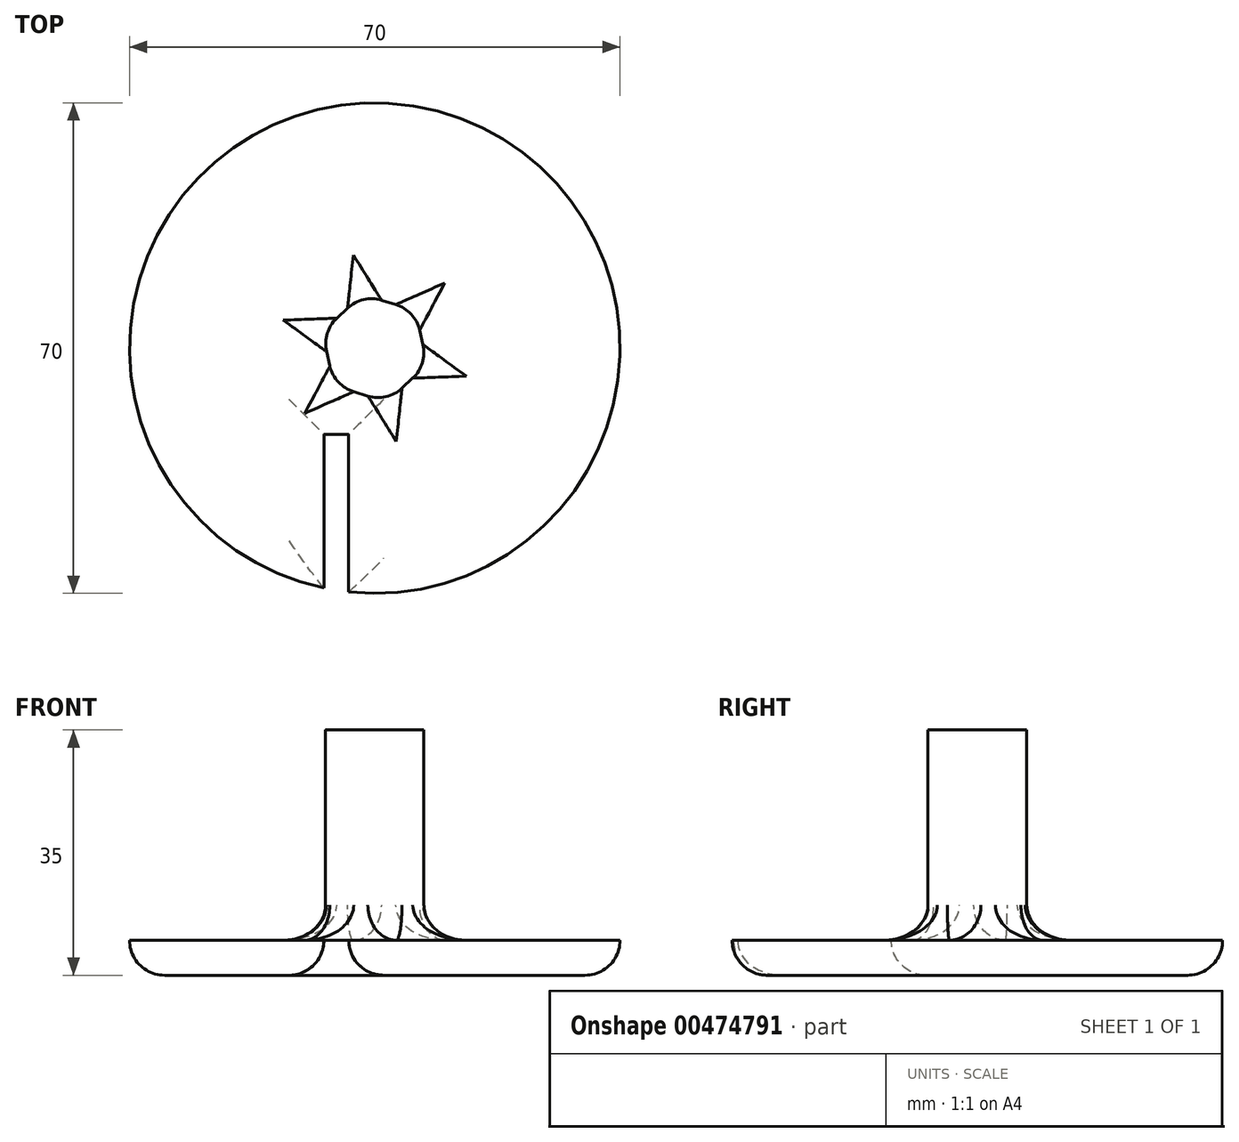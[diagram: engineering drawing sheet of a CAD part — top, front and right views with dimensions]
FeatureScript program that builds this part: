
annotation { "Feature Type Name" : "Feature", "Feature Type Description" : "" }
export const myFeature = defineFeature(function(context is Context, id is Id, definition is map)
    precondition{}
    {
        {
            var Q0;
            Q0=qCreatedBy(makeId("Top.planeOp"),FACE);
            var sketch = newSketch(context, id + "F0", { "sketchPlane" : qUnion([Q0])});
            skCircle(sketch, "E0", {"center": v(0, 0) * mm, "radius": 35 * mm});
            skSolve(sketch);
        }
        {
            var Q0;
            Q0 = qSketchRegion(id + "F0", true);
            extrude(context, id + "F1", {"entities" : qUnion([Q0]), "depth" : 5 * mm});
        }
        {
            var Q0;
            Q0=qCreatedBy(makeId("Top.planeOp"),FACE);
            var sketch = newSketch(context, id + "F2", { "sketchPlane" : qUnion([Q0])});
            skCircle(sketch, "E1.cCircle", {"center": v(0, 0) * mm, "radius": 7.88 * mm, "construction": true});
            skLineSegment(sketch, "E1.0", {"start": v(5.77, 5.37) * mm, "end": v(7.54, -2.3) * mm});
            skLineSegment(sketch, "E1.1", {"start": v(7.54, -2.3) * mm, "end": v(1.77, -7.68) * mm});
            skLineSegment(sketch, "E1.2", {"start": v(1.77, -7.68) * mm, "end": v(-5.77, -5.37) * mm});
            skLineSegment(sketch, "E1.3", {"start": v(-5.77, -5.37) * mm, "end": v(-7.54, 2.3) * mm});
            skLineSegment(sketch, "E1.4", {"start": v(-7.54, 2.3) * mm, "end": v(-1.77, 7.68) * mm});
            skLineSegment(sketch, "E1.5", {"start": v(-1.77, 7.68) * mm, "end": v(5.77, 5.37) * mm});
            skSolve(sketch);
        }
        {
            var Q0;
            Q0 = qSketchRegion(id + "F2", true);
            extrude(context, id + "F3", {"entities" : qUnion([Q0]), "operationType" : NewBodyOperationType.ADD, "depth" : 35 * mm});
        }
        {
            var Q0;
            Q0=makeQuery(id+"F1.opExtrude","CAP_FACE",FACE,{"disambiguationData":[OSD([sQuery(id+"F0.wireOp",EDGE,"E0")])],"isStart":false});
            var sketch = newSketch(context, id + "F4", { "sketchPlane" : qUnion([Q0])});
            skLineSegment(sketch, "E2.bottom", {"start": v(-3.72, -12.29) * mm, "end": v(-7.25, -12.29) * mm});
            skLineSegment(sketch, "E2.top", {"start": v(-3.72, -36.81) * mm, "end": v(-7.25, -36.81) * mm});
            skLineSegment(sketch, "E2.left", {"start": v(-3.72, -12.29) * mm, "end": v(-3.72, -36.81) * mm});
            skLineSegment(sketch, "E2.right", {"start": v(-7.25, -12.29) * mm, "end": v(-7.25, -36.81) * mm});
            skSolve(sketch);
        }
        {
            var Q0;
            Q0 = qSketchRegion(id + "F4", true);
            extrude(context, id + "F5", {"entities" : qUnion([Q0]), "operationType" : NewBodyOperationType.REMOVE, "oppositeDirection" : true, "depth" : 5 * mm});
        }
        {
            var Q0;
            Q0=makeQuery(id+"F3.boolean.opBoolean","INTERSECT",EDGE,{"derivedFrom":[makeQuery(id+"F1.opExtrude","CAP_FACE",FACE,{"disambiguationData":[OSD([sQuery(id+"F0.wireOp",EDGE,"E0")])],"isStart":false}),makeQuery(id+"F3.opExtrude","SWEPT_FACE",FACE,{"disambiguationData":[OSD([sQuery(id+"F2.wireOp",EDGE,"E1.0")])]})]});
            var Q1;
            Q1=makeQuery(id+"F3.boolean.opBoolean","INTERSECT",EDGE,{"derivedFrom":[makeQuery(id+"F1.opExtrude","CAP_FACE",FACE,{"disambiguationData":[OSD([sQuery(id+"F0.wireOp",EDGE,"E0")])],"isStart":false}),makeQuery(id+"F3.opExtrude","SWEPT_FACE",FACE,{"disambiguationData":[OSD([sQuery(id+"F2.wireOp",EDGE,"E1.1")])]})]});
            var Q2;
            Q2=makeQuery(id+"F3.boolean.opBoolean","INTERSECT",EDGE,{"derivedFrom":[makeQuery(id+"F1.opExtrude","CAP_FACE",FACE,{"disambiguationData":[OSD([sQuery(id+"F0.wireOp",EDGE,"E0")])],"isStart":false}),makeQuery(id+"F3.opExtrude","SWEPT_FACE",FACE,{"disambiguationData":[OSD([sQuery(id+"F2.wireOp",EDGE,"E1.4")])]})]});
            var Q3;
            Q3=makeQuery(id+"F3.boolean.opBoolean","INTERSECT",EDGE,{"derivedFrom":[makeQuery(id+"F1.opExtrude","CAP_FACE",FACE,{"disambiguationData":[OSD([sQuery(id+"F0.wireOp",EDGE,"E0")])],"isStart":false}),makeQuery(id+"F3.opExtrude","SWEPT_FACE",FACE,{"disambiguationData":[OSD([sQuery(id+"F2.wireOp",EDGE,"E1.3")])]})]});
            var Q4;
            Q4=makeQuery(id+"F3.boolean.opBoolean","INTERSECT",EDGE,{"derivedFrom":[makeQuery(id+"F1.opExtrude","CAP_FACE",FACE,{"disambiguationData":[OSD([sQuery(id+"F0.wireOp",EDGE,"E0")])],"isStart":false}),makeQuery(id+"F3.opExtrude","SWEPT_FACE",FACE,{"disambiguationData":[OSD([sQuery(id+"F2.wireOp",EDGE,"E1.2")])]})]});
            var Q5;
            Q5=makeQuery(id+"F1.opExtrude","CAP_FACE",FACE,{"disambiguationData":[OSD([sQuery(id+"F0.wireOp",EDGE,"E0")])],"isStart":true});
            var Q6;
            Q6=makeQuery(id+"F3.boolean.opBoolean","INTERSECT",EDGE,{"derivedFrom":[makeQuery(id+"F1.opExtrude","CAP_FACE",FACE,{"disambiguationData":[OSD([sQuery(id+"F0.wireOp",EDGE,"E0")])],"isStart":false}),makeQuery(id+"F3.opExtrude","SWEPT_FACE",FACE,{"disambiguationData":[OSD([sQuery(id+"F2.wireOp",EDGE,"E1.5")])]})]});
            fillet(context, id + "F6", {"entities" : qUnion([Q0, Q1, Q2, Q3, Q4, Q5, Q6]), "radius" : 5 * mm, "tangentPropagation" : true, "allowEdgeOverflow" : false});
        }
        {
            var Q0;
            {var subQ0=makeQuery(id+"F1.opExtrude","CAP_FACE",FACE,{"disambiguationData":[OSD([sQuery(id+"F0.wireOp",EDGE,"E0")])],"isStart":false});Q0=makeQuery(id+"F6.opFillet","BLEND_EDGE",EDGE,{"blendedFrom":[makeQuery(id+"F3.boolean.opBoolean","INTERSECT",EDGE,{"derivedFrom":[subQ0,makeQuery(id+"F3.opExtrude","SWEPT_FACE",FACE,{"disambiguationData":[OSD([sQuery(id+"F2.wireOp",EDGE,"E1.0")])]})]}),makeQuery(id+"F3.boolean.opBoolean","INTERSECT",EDGE,{"derivedFrom":[subQ0,makeQuery(id+"F3.opExtrude","SWEPT_FACE",FACE,{"disambiguationData":[OSD([sQuery(id+"F2.wireOp",EDGE,"E1.1")])]})]})],"blendedInto":[]});}
            var Q1;
            {var subQ0=makeQuery(id+"F1.opExtrude","CAP_FACE",FACE,{"disambiguationData":[OSD([sQuery(id+"F0.wireOp",EDGE,"E0")])],"isStart":false});Q1=makeQuery(id+"F6.opFillet","BLEND_EDGE",EDGE,{"blendedFrom":[makeQuery(id+"F3.boolean.opBoolean","INTERSECT",EDGE,{"derivedFrom":[subQ0,makeQuery(id+"F3.opExtrude","SWEPT_FACE",FACE,{"disambiguationData":[OSD([sQuery(id+"F2.wireOp",EDGE,"E1.0")])]})]}),makeQuery(id+"F3.boolean.opBoolean","INTERSECT",EDGE,{"derivedFrom":[subQ0,makeQuery(id+"F3.opExtrude","SWEPT_FACE",FACE,{"disambiguationData":[OSD([sQuery(id+"F2.wireOp",EDGE,"E1.5")])]})]})],"blendedInto":[]});}
            var Q2;
            {var subQ0=makeQuery(id+"F1.opExtrude","CAP_FACE",FACE,{"disambiguationData":[OSD([sQuery(id+"F0.wireOp",EDGE,"E0")])],"isStart":false});Q2=makeQuery(id+"F6.opFillet","BLEND_EDGE",EDGE,{"blendedFrom":[makeQuery(id+"F3.boolean.opBoolean","INTERSECT",EDGE,{"derivedFrom":[subQ0,makeQuery(id+"F3.opExtrude","SWEPT_FACE",FACE,{"disambiguationData":[OSD([sQuery(id+"F2.wireOp",EDGE,"E1.4")])]})]}),makeQuery(id+"F3.boolean.opBoolean","INTERSECT",EDGE,{"derivedFrom":[subQ0,makeQuery(id+"F3.opExtrude","SWEPT_FACE",FACE,{"disambiguationData":[OSD([sQuery(id+"F2.wireOp",EDGE,"E1.5")])]})]})],"blendedInto":[]});}
            var Q3;
            {var subQ0=makeQuery(id+"F1.opExtrude","CAP_FACE",FACE,{"disambiguationData":[OSD([sQuery(id+"F0.wireOp",EDGE,"E0")])],"isStart":false});Q3=makeQuery(id+"F6.opFillet","BLEND_EDGE",EDGE,{"blendedFrom":[makeQuery(id+"F3.boolean.opBoolean","INTERSECT",EDGE,{"derivedFrom":[subQ0,makeQuery(id+"F3.opExtrude","SWEPT_FACE",FACE,{"disambiguationData":[OSD([sQuery(id+"F2.wireOp",EDGE,"E1.3")])]})]}),makeQuery(id+"F3.boolean.opBoolean","INTERSECT",EDGE,{"derivedFrom":[subQ0,makeQuery(id+"F3.opExtrude","SWEPT_FACE",FACE,{"disambiguationData":[OSD([sQuery(id+"F2.wireOp",EDGE,"E1.4")])]})]})],"blendedInto":[]});}
            fillet(context, id + "F7", {"entities" : qUnion([Q0, Q1, Q2, Q3]), "radius" : 5 * mm, "tangentPropagation" : true, "allowEdgeOverflow" : false});
        }
        {
            var Q0;
            {var subQ0=makeQuery(id+"F1.opExtrude","CAP_FACE",FACE,{"disambiguationData":[OSD([sQuery(id+"F0.wireOp",EDGE,"E0")])],"isStart":false});Q0=makeQuery(id+"F6.opFillet","BLEND_EDGE",EDGE,{"blendedFrom":[makeQuery(id+"F3.boolean.opBoolean","INTERSECT",EDGE,{"derivedFrom":[subQ0,makeQuery(id+"F3.opExtrude","SWEPT_FACE",FACE,{"disambiguationData":[OSD([sQuery(id+"F2.wireOp",EDGE,"E1.1")])]})]}),makeQuery(id+"F3.boolean.opBoolean","INTERSECT",EDGE,{"derivedFrom":[subQ0,makeQuery(id+"F3.opExtrude","SWEPT_FACE",FACE,{"disambiguationData":[OSD([sQuery(id+"F2.wireOp",EDGE,"E1.2")])]})]})],"blendedInto":[]});}
            var Q1;
            {var subQ0=sQuery(id+"F2.wireOp",EDGE,"E1.0");var subQ1=sQuery(id+"F0.wireOp",EDGE,"E0");var subQ2=makeQuery(id+"F1.opExtrude","CAP_FACE",FACE,{"disambiguationData":[OSD([subQ1])],"isStart":false});Q1=makeQuery(id+"F7.opFillet","BLEND_EDGE",EDGE,{"blendedFrom":[makeQuery(id+"F6.opFillet","BLEND_EDGE",EDGE,{"blendedFrom":[makeQuery(id+"F3.boolean.opBoolean","INTERSECT",EDGE,{"derivedFrom":[subQ2,makeQuery(id+"F3.opExtrude","SWEPT_FACE",FACE,{"disambiguationData":[OSD([subQ0])]})]}),makeQuery(id+"F3.boolean.opBoolean","INTERSECT",EDGE,{"derivedFrom":[subQ2,makeQuery(id+"F3.opExtrude","SWEPT_FACE",FACE,{"disambiguationData":[OSD([sQuery(id+"F2.wireOp",EDGE,"E1.1")])]})]})],"blendedInto":[]}),makeQuery(id+"F6.opFillet","BLEND_FACE",FACE,{"disambiguationData":[OSD([subQ1,subQ0])]})],"blendedInto":[makeQuery(id+"F6.opFillet","BLEND_FACE",FACE,{"disambiguationData":[OSD([subQ1,subQ0])]})]});}
            var Q2;
            {var subQ0=sQuery(id+"F2.wireOp",EDGE,"E1.5");var subQ1=sQuery(id+"F0.wireOp",EDGE,"E0");var subQ2=makeQuery(id+"F1.opExtrude","CAP_FACE",FACE,{"disambiguationData":[OSD([subQ1])],"isStart":false});Q2=makeQuery(id+"F7.opFillet","BLEND_EDGE",EDGE,{"blendedFrom":[makeQuery(id+"F6.opFillet","BLEND_EDGE",EDGE,{"blendedFrom":[makeQuery(id+"F3.boolean.opBoolean","INTERSECT",EDGE,{"derivedFrom":[subQ2,makeQuery(id+"F3.opExtrude","SWEPT_FACE",FACE,{"disambiguationData":[OSD([sQuery(id+"F2.wireOp",EDGE,"E1.0")])]})]}),makeQuery(id+"F3.boolean.opBoolean","INTERSECT",EDGE,{"derivedFrom":[subQ2,makeQuery(id+"F3.opExtrude","SWEPT_FACE",FACE,{"disambiguationData":[OSD([subQ0])]})]})],"blendedInto":[]}),makeQuery(id+"F6.opFillet","BLEND_FACE",FACE,{"disambiguationData":[OSD([subQ1,subQ0])]})],"blendedInto":[makeQuery(id+"F6.opFillet","BLEND_FACE",FACE,{"disambiguationData":[OSD([subQ1,subQ0])]})]});}
            var Q3;
            {var subQ0=sQuery(id+"F2.wireOp",EDGE,"E1.4");var subQ1=sQuery(id+"F0.wireOp",EDGE,"E0");var subQ2=makeQuery(id+"F1.opExtrude","CAP_FACE",FACE,{"disambiguationData":[OSD([subQ1])],"isStart":false});Q3=makeQuery(id+"F7.opFillet","BLEND_EDGE",EDGE,{"blendedFrom":[makeQuery(id+"F6.opFillet","BLEND_EDGE",EDGE,{"blendedFrom":[makeQuery(id+"F3.boolean.opBoolean","INTERSECT",EDGE,{"derivedFrom":[subQ2,makeQuery(id+"F3.opExtrude","SWEPT_FACE",FACE,{"disambiguationData":[OSD([subQ0])]})]}),makeQuery(id+"F3.boolean.opBoolean","INTERSECT",EDGE,{"derivedFrom":[subQ2,makeQuery(id+"F3.opExtrude","SWEPT_FACE",FACE,{"disambiguationData":[OSD([sQuery(id+"F2.wireOp",EDGE,"E1.5")])]})]})],"blendedInto":[]}),makeQuery(id+"F6.opFillet","BLEND_FACE",FACE,{"disambiguationData":[OSD([subQ1,subQ0])]})],"blendedInto":[makeQuery(id+"F6.opFillet","BLEND_FACE",FACE,{"disambiguationData":[OSD([subQ1,subQ0])]})]});}
            var Q4;
            {var subQ0=sQuery(id+"F2.wireOp",EDGE,"E1.3");var subQ1=sQuery(id+"F0.wireOp",EDGE,"E0");var subQ2=makeQuery(id+"F1.opExtrude","CAP_FACE",FACE,{"disambiguationData":[OSD([subQ1])],"isStart":false});Q4=makeQuery(id+"F7.opFillet","BLEND_EDGE",EDGE,{"blendedFrom":[makeQuery(id+"F6.opFillet","BLEND_EDGE",EDGE,{"blendedFrom":[makeQuery(id+"F3.boolean.opBoolean","INTERSECT",EDGE,{"derivedFrom":[subQ2,makeQuery(id+"F3.opExtrude","SWEPT_FACE",FACE,{"disambiguationData":[OSD([subQ0])]})]}),makeQuery(id+"F3.boolean.opBoolean","INTERSECT",EDGE,{"derivedFrom":[subQ2,makeQuery(id+"F3.opExtrude","SWEPT_FACE",FACE,{"disambiguationData":[OSD([sQuery(id+"F2.wireOp",EDGE,"E1.4")])]})]})],"blendedInto":[]}),makeQuery(id+"F6.opFillet","BLEND_FACE",FACE,{"disambiguationData":[OSD([subQ1,subQ0])]})],"blendedInto":[makeQuery(id+"F6.opFillet","BLEND_FACE",FACE,{"disambiguationData":[OSD([subQ1,subQ0])]})]});}
            var Q5;
            {var subQ0=makeQuery(id+"F1.opExtrude","CAP_FACE",FACE,{"disambiguationData":[OSD([sQuery(id+"F0.wireOp",EDGE,"E0")])],"isStart":false});Q5=makeQuery(id+"F6.opFillet","BLEND_EDGE",EDGE,{"blendedFrom":[makeQuery(id+"F3.boolean.opBoolean","INTERSECT",EDGE,{"derivedFrom":[subQ0,makeQuery(id+"F3.opExtrude","SWEPT_FACE",FACE,{"disambiguationData":[OSD([sQuery(id+"F2.wireOp",EDGE,"E1.2")])]})]}),makeQuery(id+"F3.boolean.opBoolean","INTERSECT",EDGE,{"derivedFrom":[subQ0,makeQuery(id+"F3.opExtrude","SWEPT_FACE",FACE,{"disambiguationData":[OSD([sQuery(id+"F2.wireOp",EDGE,"E1.3")])]})]})],"blendedInto":[]});}
            fillet(context, id + "F8", {"entities" : qUnion([Q0, Q1, Q2, Q3, Q4, Q5]), "radius" : 5 * mm, "tangentPropagation" : true, "allowEdgeOverflow" : false});
        }
    });
